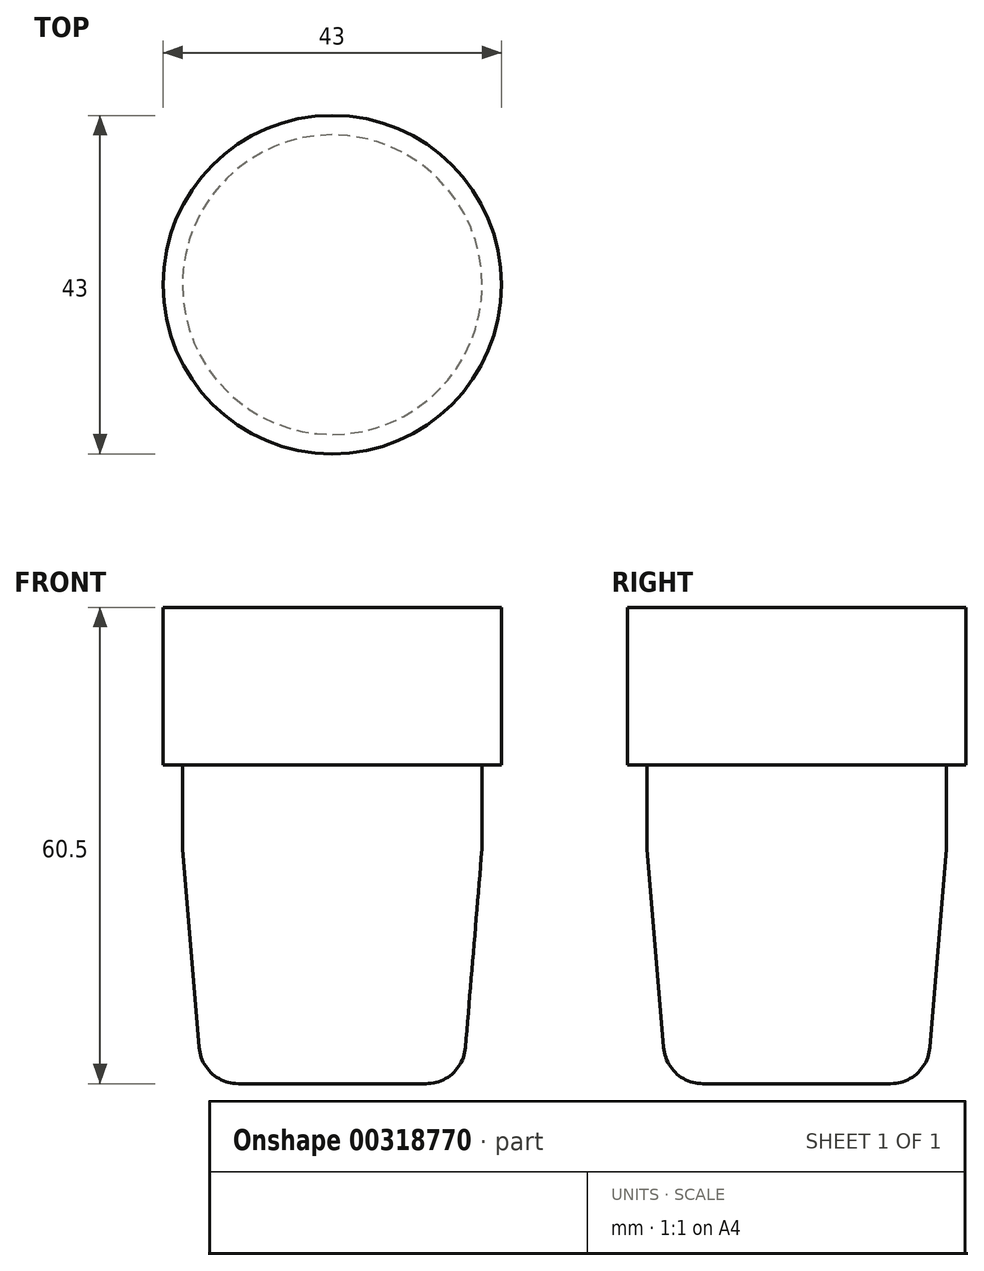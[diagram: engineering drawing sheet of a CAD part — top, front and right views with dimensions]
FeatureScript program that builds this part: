
annotation { "Feature Type Name" : "Feature", "Feature Type Description" : "" }
export const myFeature = defineFeature(function(context is Context, id is Id, definition is map)
    precondition{}
    {
        {
            var Q0;
            Q0=qCreatedBy(makeId("Top.planeOp"),FACE);
            var sketch = newSketch(context, id + "F0", { "sketchPlane" : qUnion([Q0])});
            skCircle(sketch, "E0", {"center": v(0, 0) * mm, "radius": 21.5 * mm});
            skSolve(sketch);
        }
        {
            var Q0;
            Q0=makeQuery(id+"F0.imprint","IMPRINT",FACE,{"disambiguationData":[TD([[makeQuery(id+"F0.imprint","IMPRINT",EDGE,{"derivedFrom":sQuery(id+"F0.wireOp",EDGE,"E0")}),1.0]])]});
            extrude(context, id + "F1", {"entities" : qUnion([Q0]), "depth" : 20 * mm, "offsetDistance" : 25 * mm});
        }
        {
            var Q0;
            Q0=makeQuery(id+"F1.opExtrude","CAP_FACE",FACE,{"disambiguationData":[OSD([sQuery(id+"F0.wireOp",EDGE,"E0")])],"isStart":true});
            var sketch = newSketch(context, id + "F2", { "sketchPlane" : qUnion([Q0])});
            skCircle(sketch, "E1", {"center": v(0, 0) * mm, "radius": 19.03 * mm});
            skSolve(sketch);
        }
        {
            var Q0;
            Q0=makeQuery(id+"F2.imprint","IMPRINT",FACE,{"disambiguationData":[TD([[makeQuery(id+"F2.imprint","IMPRINT",EDGE,{"derivedFrom":sQuery(id+"F2.wireOp",EDGE,"E1")}),1.0]])]});
            extrude(context, id + "F3", {"entities" : qUnion([Q0]), "operationType" : NewBodyOperationType.ADD, "depth" : 0.5 * mm, "offsetDistance" : 25 * mm});
        }
        {
            var Q0;
            Q0=makeQuery(id+"F3.opExtrude","CAP_FACE",FACE,{"disambiguationData":[OSD([sQuery(id+"F2.wireOp",EDGE,"E1")])],"isStart":false});
            var sketch = newSketch(context, id + "F4", { "sketchPlane" : qUnion([Q0])});
            skCircle(sketch, "E2", {"center": v(0, 0) * mm, "radius": 21.67 * mm});
            skSolve(sketch);
        }
        {
            var Q0;
            Q0=makeQuery(id+"F4.imprint","IMPRINT",FACE,{"disambiguationData":[TD([[makeQuery(id+"F4.imprint","IMPRINT",EDGE,{"derivedFrom":makeQuery(id+"F3.opExtrude","CAP_EDGE",EDGE,{"disambiguationData":[OSD([sQuery(id+"F2.wireOp",EDGE,"E1")])],"isStart":false})}),1.0]])]});
            extrude(context, id + "F5", {"entities" : qUnion([Q0]), "operationType" : NewBodyOperationType.ADD, "depth" : 40 * mm, "offsetDistance" : 25 * mm});
        }
        {
            var Q0;
            Q0=makeQuery(id+"F5.opExtrude","CAP_EDGE",EDGE,{"disambiguationData":[OSD([sQuery(id+"F2.wireOp",EDGE,"E1")])],"isStart":false});
            chamfer(context, id + "F6", {"entities" : qUnion([Q0]), "chamferType" : ChamferType.TWO_OFFSETS, "width1" : 2.5 * mm, "oppositeDirection" : false, "width2" : 30 * mm, "tangentPropagation" : true});
        }
        {
            var Q0;
            {var subQ0=sQuery(id+"F2.wireOp",EDGE,"E1");Q0=makeQuery(id+"F6.opChamfer","BLEND_EDGE",EDGE,{"blendedFrom":[makeQuery(id+"F5.opExtrude","CAP_EDGE",EDGE,{"disambiguationData":[OSD([subQ0])],"isStart":false}),makeQuery(id+"F5.opExtrude","CAP_FACE",FACE,{"disambiguationData":[OSD([subQ0])],"isStart":false})],"blendedInto":[makeQuery(id+"F5.opExtrude","CAP_FACE",FACE,{"disambiguationData":[OSD([subQ0])],"isStart":false})]});}
            var Q1;
            {var subQ0=sQuery(id+"F2.wireOp",EDGE,"E1");Q1=makeQuery(id+"F6.opChamfer","BLEND_EDGE",EDGE,{"blendedFrom":[makeQuery(id+"F5.opExtrude","CAP_EDGE",EDGE,{"disambiguationData":[OSD([subQ0])],"isStart":false}),makeQuery(id+"F5.boolean.opBoolean","MERGE",FACE,{"derivedFrom":[makeQuery(id+"F3.opExtrude","SWEPT_FACE",FACE,{"disambiguationData":[OSD([subQ0])]}),makeQuery(id+"F5.opExtrude","SWEPT_FACE",FACE,{"disambiguationData":[OSD([subQ0])]})]})],"blendedInto":[makeQuery(id+"F5.boolean.opBoolean","MERGE",FACE,{"derivedFrom":[makeQuery(id+"F3.opExtrude","SWEPT_FACE",FACE,{"disambiguationData":[OSD([subQ0])]}),makeQuery(id+"F5.opExtrude","SWEPT_FACE",FACE,{"disambiguationData":[OSD([subQ0])]})]})]});}
            fillet(context, id + "F7", {"entities" : qUnion([Q0, Q1]), "radius" : 5 * mm, "tangentPropagation" : true, "allowEdgeOverflow" : false});
        }
    });
